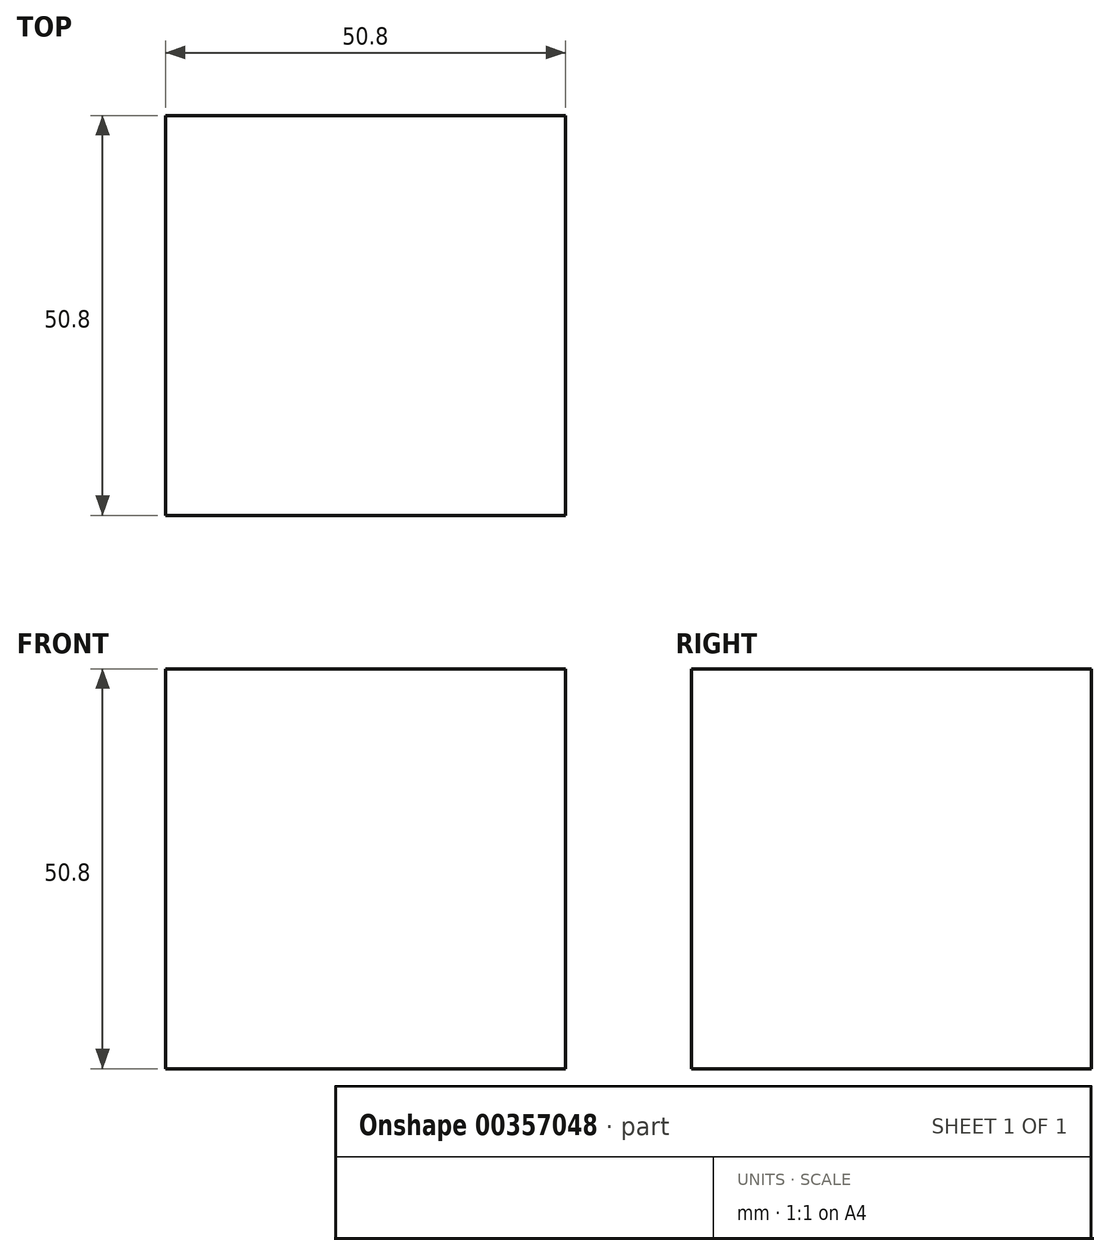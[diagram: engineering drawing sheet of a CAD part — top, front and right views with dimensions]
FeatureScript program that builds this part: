
annotation { "Feature Type Name" : "Feature", "Feature Type Description" : "" }
export const myFeature = defineFeature(function(context is Context, id is Id, definition is map)
    precondition{}
    {
        {
            var Q0;
            Q0=qCreatedBy(makeId("Front.planeOp"),FACE);
            var sketch = newSketch(context, id + "F0", { "sketchPlane" : qUnion([Q0])});
            skLineSegment(sketch, "E0", {"start": v(0, 0) * mm, "end": v(50.8, 0) * mm});
            skLineSegment(sketch, "E1", {"start": v(50.8, 0) * mm, "end": v(50.8, 50.8) * mm});
            skLineSegment(sketch, "E2", {"start": v(50.8, 50.8) * mm, "end": v(0, 50.8) * mm});
            skLineSegment(sketch, "E3", {"start": v(0, 50.8) * mm, "end": v(0, 0) * mm});
            skSolve(sketch);
        }
        {
            var Q0;
            Q0=makeQuery(id+"F0.imprint","IMPRINT",FACE,{"disambiguationData":[TD([[makeQuery(id+"F0.imprint","IMPRINT",EDGE,{"derivedFrom":sQuery(id+"F0.wireOp",EDGE,"E0")}),1.0]])]});
            extrude(context, id + "F1", {"entities" : qUnion([Q0]), "depth" : 50.8 * mm});
        }
    });
